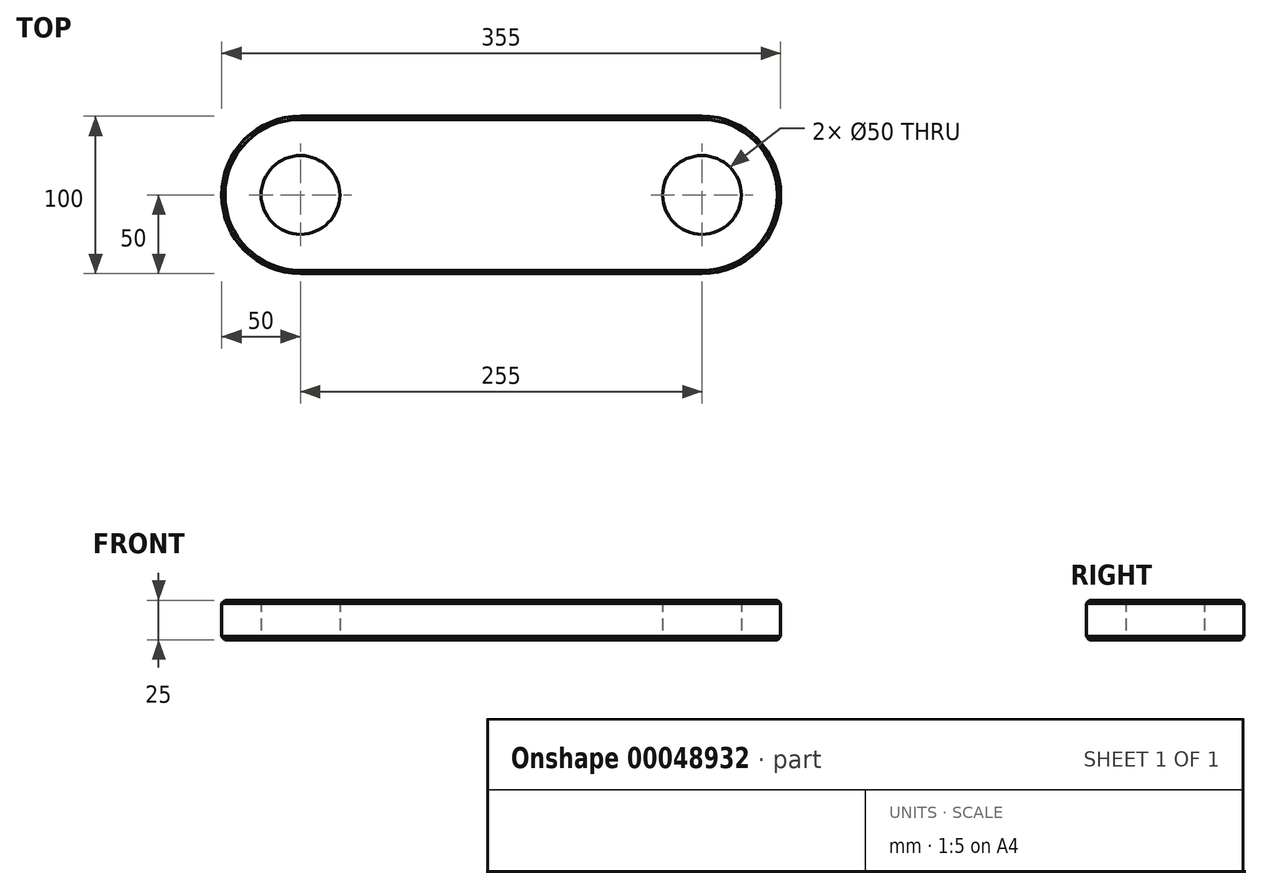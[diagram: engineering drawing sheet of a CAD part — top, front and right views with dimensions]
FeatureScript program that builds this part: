
annotation { "Feature Type Name" : "Feature", "Feature Type Description" : "" }
export const myFeature = defineFeature(function(context is Context, id is Id, definition is map)
    precondition{}
    {
        {
            var Q0;
            Q0=qCreatedBy(makeId("Top.planeOp"),FACE);
            var sketch = newSketch(context, id + "F0", { "sketchPlane" : qUnion([Q0])});
            skArc(sketch, "E0", {"start": v(0, -50) * mm, "mid": v(50, 0) * mm, "end": v(0, 50) * mm});
            skCircle(sketch, "E1", {"center": v(0, 0) * mm, "radius": 25 * mm});
            skLineSegment(sketch, "E2", {"start": v(0, 0) * mm, "end": v(-255, 0) * mm, "construction": true});
            skCircle(sketch, "E3", {"center": v(-255, 0) * mm, "radius": 25 * mm});
            skArc(sketch, "E4", {"start": v(-255, 50) * mm, "mid": v(-305, 0) * mm, "end": v(-255, -50) * mm});
            skLineSegment(sketch, "E5", {"start": v(-255, 50) * mm, "end": v(0, 50) * mm});
            skLineSegment(sketch, "E6", {"start": v(-255, -50) * mm, "end": v(0, -50) * mm});
            skSolve(sketch);
        }
        {
            var Q0;
            Q0=makeQuery(id+"F0.imprint","IMPRINT",FACE,{"disambiguationData":[TD([[makeQuery(id+"F0.imprint","IMPRINT",EDGE,{"derivedFrom":sQuery(id+"F0.wireOp",EDGE,"E0")}),1.0]])]});
            extrude(context, id + "F1", {"entities" : qUnion([Q0]), "depth" : 25 * mm});
        }
        {
            var Q0;
            Q0=makeQuery(id+"F1.opExtrude","CAP_EDGE",EDGE,{"disambiguationData":[OSD([sQuery(id+"F0.wireOp",EDGE,"E0")])],"isStart":false});
            var Q1;
            Q1=makeQuery(id+"F1.opExtrude","CAP_EDGE",EDGE,{"disambiguationData":[OSD([sQuery(id+"F0.wireOp",EDGE,"E0")])],"isStart":true});
            chamfer(context, id + "F2", {"entities" : qUnion([Q0, Q1]), "chamferType" : ChamferType.OFFSET_ANGLE, "width" : 2 * mm, "oppositeDirection" : false, "angle" : 45 * degree, "tangentPropagation" : true});
        }
    });
